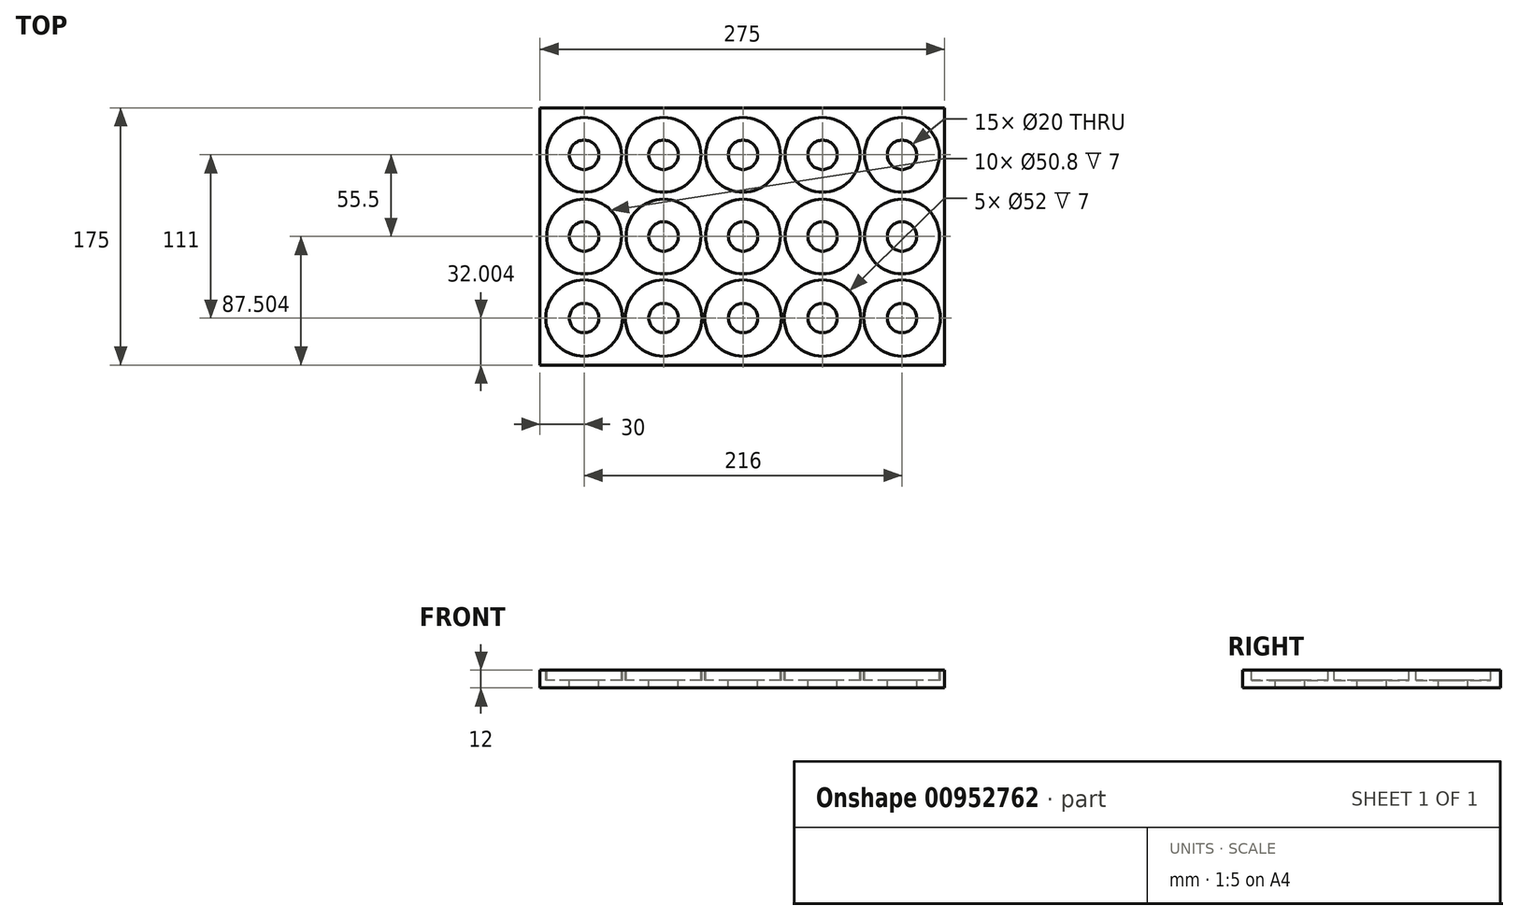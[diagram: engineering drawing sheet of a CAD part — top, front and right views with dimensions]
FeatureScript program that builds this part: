
annotation { "Feature Type Name" : "Feature", "Feature Type Description" : "" }
export const myFeature = defineFeature(function(context is Context, id is Id, definition is map)
    precondition{}
    {
        {
            var Q0;
            Q0=qCreatedBy(makeId("Top.planeOp"),FACE);
            var sketch = newSketch(context, id + "F0", { "sketchPlane" : qUnion([Q0])});
            skLineSegment(sketch, "E0.bottom", {"start": v(-57.94, 136.27) * mm, "end": v(217.06, 136.27) * mm});
            skLineSegment(sketch, "E0.top", {"start": v(-57.94, -38.73) * mm, "end": v(217.06, -38.73) * mm});
            skLineSegment(sketch, "E0.left", {"start": v(-57.94, 136.27) * mm, "end": v(-57.94, -38.73) * mm});
            skLineSegment(sketch, "E0.right", {"start": v(217.06, 136.27) * mm, "end": v(217.06, -38.73) * mm});
            skSolve(sketch);
        }
        {
            var Q0;
            Q0 = qSketchRegion(id + "F0", true);
            extrude(context, id + "F1", {"entities" : qUnion([Q0]), "depth" : 12 * mm, "offsetDistance" : 25 * mm});
        }
        {
            var Q0;
            Q0=makeQuery(id+"F1.opExtrude","CAP_FACE",FACE,{"disambiguationData":[OSD([sQuery(id+"F0.wireOp",EDGE,"E0.bottom"),sQuery(id+"F0.wireOp",EDGE,"E0.top"),sQuery(id+"F0.wireOp",EDGE,"E0.left"),sQuery(id+"F0.wireOp",EDGE,"E0.right")])],"isStart":false});
            var sketch = newSketch(context, id + "F2", { "sketchPlane" : qUnion([Q0])});
            skCircle(sketch, "E1", {"center": v(-27.94, 104.27) * mm, "radius": 25.4 * mm});
            skCircle(sketch, "E2", {"center": v(-27.94, 48.77) * mm, "radius": 25.4 * mm});
            skPoint(sketch, "E2.centerSnap0", {"position": v(-57.94, 48.77) * mm});
            skCircle(sketch, "E3", {"center": v(-27.94, -6.73) * mm, "radius": 26 * mm});
            skCircle(sketch, "E4", {"center": v(26.06, 104.27) * mm, "radius": 25.4 * mm});
            skCircle(sketch, "E5", {"center": v(26.06, 48.77) * mm, "radius": 25.4 * mm});
            skCircle(sketch, "E6", {"center": v(26.06, -6.73) * mm, "radius": 26 * mm});
            skCircle(sketch, "E7", {"center": v(80.06, 104.27) * mm, "radius": 25.4 * mm});
            skCircle(sketch, "E8", {"center": v(80.06, 48.77) * mm, "radius": 25.4 * mm});
            skCircle(sketch, "E9", {"center": v(80.06, -6.73) * mm, "radius": 26 * mm});
            skCircle(sketch, "E10", {"center": v(134.06, 104.27) * mm, "radius": 25.4 * mm});
            skCircle(sketch, "E11", {"center": v(134.06, 48.77) * mm, "radius": 25.4 * mm});
            skCircle(sketch, "E12", {"center": v(134.06, -6.73) * mm, "radius": 26 * mm});
            skCircle(sketch, "E13", {"center": v(188.06, 104.27) * mm, "radius": 25.4 * mm});
            skCircle(sketch, "E14", {"center": v(188.06, 48.77) * mm, "radius": 25.4 * mm});
            skCircle(sketch, "E15", {"center": v(188.06, -6.73) * mm, "radius": 26 * mm});
            skCircle(sketch, "E16", {"center": v(-27.94, 104.27) * mm, "radius": 10 * mm});
            skCircle(sketch, "E17", {"center": v(-27.94, 48.77) * mm, "radius": 10 * mm});
            skCircle(sketch, "E18", {"center": v(-27.94, -6.73) * mm, "radius": 10 * mm});
            skCircle(sketch, "E19", {"center": v(26.06, -6.73) * mm, "radius": 10 * mm});
            skCircle(sketch, "E20", {"center": v(26.06, 48.77) * mm, "radius": 10 * mm});
            skCircle(sketch, "E21", {"center": v(26.06, 104.27) * mm, "radius": 10 * mm});
            skCircle(sketch, "E22", {"center": v(80.06, 104.27) * mm, "radius": 10 * mm});
            skCircle(sketch, "E23", {"center": v(80.06, 48.77) * mm, "radius": 10 * mm});
            skCircle(sketch, "E24", {"center": v(80.06, -6.73) * mm, "radius": 10 * mm});
            skCircle(sketch, "E25", {"center": v(134.06, -6.73) * mm, "radius": 10 * mm});
            skCircle(sketch, "E26", {"center": v(188.06, -6.73) * mm, "radius": 10 * mm});
            skCircle(sketch, "E27", {"center": v(188.06, 48.77) * mm, "radius": 10 * mm});
            skCircle(sketch, "E28", {"center": v(134.06, 48.77) * mm, "radius": 10 * mm});
            skCircle(sketch, "E29", {"center": v(134.06, 104.27) * mm, "radius": 10 * mm});
            skCircle(sketch, "E30", {"center": v(188.06, 104.27) * mm, "radius": 10 * mm});
            skSolve(sketch);
        }
        {
            var Q0;
            Q0=makeQuery(id+"F2.imprint","IMPRINT",FACE,{"disambiguationData":[TD([[makeQuery(id+"F2.imprint","IMPRINT",EDGE,{"derivedFrom":sQuery(id+"F2.wireOp",EDGE,"E1")}),1.0]])]});
            var Q1;
            Q1=makeQuery(id+"F2.imprint","IMPRINT",FACE,{"disambiguationData":[TD([[makeQuery(id+"F2.imprint","IMPRINT",EDGE,{"derivedFrom":sQuery(id+"F2.wireOp",EDGE,"E2")}),1.0]])]});
            var Q2;
            Q2=makeQuery(id+"F2.imprint","IMPRINT",FACE,{"disambiguationData":[TD([[makeQuery(id+"F2.imprint","IMPRINT",EDGE,{"derivedFrom":sQuery(id+"F2.wireOp",EDGE,"E3")}),1.0]])]});
            var Q3;
            Q3=makeQuery(id+"F2.imprint","IMPRINT",FACE,{"disambiguationData":[TD([[makeQuery(id+"F2.imprint","IMPRINT",EDGE,{"derivedFrom":sQuery(id+"F2.wireOp",EDGE,"E6")}),1.0]])]});
            var Q4;
            Q4=makeQuery(id+"F2.imprint","IMPRINT",FACE,{"disambiguationData":[TD([[makeQuery(id+"F2.imprint","IMPRINT",EDGE,{"derivedFrom":sQuery(id+"F2.wireOp",EDGE,"E5")}),1.0]])]});
            var Q5;
            Q5=makeQuery(id+"F2.imprint","IMPRINT",FACE,{"disambiguationData":[TD([[makeQuery(id+"F2.imprint","IMPRINT",EDGE,{"derivedFrom":sQuery(id+"F2.wireOp",EDGE,"E4")}),1.0]])]});
            var Q6;
            Q6=makeQuery(id+"F2.imprint","IMPRINT",FACE,{"disambiguationData":[TD([[makeQuery(id+"F2.imprint","IMPRINT",EDGE,{"derivedFrom":sQuery(id+"F2.wireOp",EDGE,"E7")}),1.0]])]});
            var Q7;
            Q7=makeQuery(id+"F2.imprint","IMPRINT",FACE,{"disambiguationData":[TD([[makeQuery(id+"F2.imprint","IMPRINT",EDGE,{"derivedFrom":sQuery(id+"F2.wireOp",EDGE,"E8")}),1.0]])]});
            var Q8;
            Q8=makeQuery(id+"F2.imprint","IMPRINT",FACE,{"disambiguationData":[TD([[makeQuery(id+"F2.imprint","IMPRINT",EDGE,{"derivedFrom":sQuery(id+"F2.wireOp",EDGE,"E9")}),1.0]])]});
            var Q9;
            Q9=makeQuery(id+"F2.imprint","IMPRINT",FACE,{"disambiguationData":[TD([[makeQuery(id+"F2.imprint","IMPRINT",EDGE,{"derivedFrom":sQuery(id+"F2.wireOp",EDGE,"E12")}),1.0]])]});
            var Q10;
            Q10=makeQuery(id+"F2.imprint","IMPRINT",FACE,{"disambiguationData":[TD([[makeQuery(id+"F2.imprint","IMPRINT",EDGE,{"derivedFrom":sQuery(id+"F2.wireOp",EDGE,"E11")}),1.0]])]});
            var Q11;
            Q11=makeQuery(id+"F2.imprint","IMPRINT",FACE,{"disambiguationData":[TD([[makeQuery(id+"F2.imprint","IMPRINT",EDGE,{"derivedFrom":sQuery(id+"F2.wireOp",EDGE,"E10")}),1.0]])]});
            var Q12;
            Q12=makeQuery(id+"F2.imprint","IMPRINT",FACE,{"disambiguationData":[TD([[makeQuery(id+"F2.imprint","IMPRINT",EDGE,{"derivedFrom":sQuery(id+"F2.wireOp",EDGE,"E13")}),1.0]])]});
            var Q13;
            Q13=makeQuery(id+"F2.imprint","IMPRINT",FACE,{"disambiguationData":[TD([[makeQuery(id+"F2.imprint","IMPRINT",EDGE,{"derivedFrom":sQuery(id+"F2.wireOp",EDGE,"E14")}),1.0]])]});
            var Q14;
            Q14=makeQuery(id+"F2.imprint","IMPRINT",FACE,{"disambiguationData":[TD([[makeQuery(id+"F2.imprint","IMPRINT",EDGE,{"derivedFrom":sQuery(id+"F2.wireOp",EDGE,"E15")}),1.0]])]});
            extrude(context, id + "F3", {"entities" : qUnion([Q0, Q1, Q2, Q3, Q4, Q5, Q6, Q7, Q8, Q9, Q10, Q11, Q12, Q13, Q14]), "operationType" : NewBodyOperationType.REMOVE, "oppositeDirection" : true, "depth" : 7 * mm, "offsetDistance" : 25 * mm});
        }
        {
            var Q0;
            Q0=makeQuery(id+"F3.boolean.opBoolean","SPLIT",FACE,{"disambiguationData":[TD([makeQuery(id+"F3.opExtrude","SWEPT_FACE",FACE,{"disambiguationData":[OSD([sQuery(id+"F2.wireOp",EDGE,"E16")])]})])],"derivedFrom":makeQuery(id+"F1.opExtrude","CAP_FACE",FACE,{"disambiguationData":[OSD([sQuery(id+"F0.wireOp",EDGE,"E0.bottom"),sQuery(id+"F0.wireOp",EDGE,"E0.top"),sQuery(id+"F0.wireOp",EDGE,"E0.left"),sQuery(id+"F0.wireOp",EDGE,"E0.right")])],"isStart":false})});
            var Q1;
            Q1=makeQuery(id+"F3.boolean.opBoolean","SPLIT",FACE,{"disambiguationData":[TD([makeQuery(id+"F3.opExtrude","SWEPT_FACE",FACE,{"disambiguationData":[OSD([sQuery(id+"F2.wireOp",EDGE,"E21")])]})])],"derivedFrom":makeQuery(id+"F1.opExtrude","CAP_FACE",FACE,{"disambiguationData":[OSD([sQuery(id+"F0.wireOp",EDGE,"E0.bottom"),sQuery(id+"F0.wireOp",EDGE,"E0.top"),sQuery(id+"F0.wireOp",EDGE,"E0.left"),sQuery(id+"F0.wireOp",EDGE,"E0.right")])],"isStart":false})});
            var Q2;
            Q2=makeQuery(id+"F3.boolean.opBoolean","SPLIT",FACE,{"disambiguationData":[TD([makeQuery(id+"F3.opExtrude","SWEPT_FACE",FACE,{"disambiguationData":[OSD([sQuery(id+"F2.wireOp",EDGE,"E22")])]})])],"derivedFrom":makeQuery(id+"F1.opExtrude","CAP_FACE",FACE,{"disambiguationData":[OSD([sQuery(id+"F0.wireOp",EDGE,"E0.bottom"),sQuery(id+"F0.wireOp",EDGE,"E0.top"),sQuery(id+"F0.wireOp",EDGE,"E0.left"),sQuery(id+"F0.wireOp",EDGE,"E0.right")])],"isStart":false})});
            var Q3;
            Q3=makeQuery(id+"F3.boolean.opBoolean","SPLIT",FACE,{"disambiguationData":[TD([makeQuery(id+"F3.opExtrude","SWEPT_FACE",FACE,{"disambiguationData":[OSD([sQuery(id+"F2.wireOp",EDGE,"E29")])]})])],"derivedFrom":makeQuery(id+"F1.opExtrude","CAP_FACE",FACE,{"disambiguationData":[OSD([sQuery(id+"F0.wireOp",EDGE,"E0.bottom"),sQuery(id+"F0.wireOp",EDGE,"E0.top"),sQuery(id+"F0.wireOp",EDGE,"E0.left"),sQuery(id+"F0.wireOp",EDGE,"E0.right")])],"isStart":false})});
            var Q4;
            Q4=makeQuery(id+"F3.boolean.opBoolean","SPLIT",FACE,{"disambiguationData":[TD([makeQuery(id+"F3.opExtrude","SWEPT_FACE",FACE,{"disambiguationData":[OSD([sQuery(id+"F2.wireOp",EDGE,"E30")])]})])],"derivedFrom":makeQuery(id+"F1.opExtrude","CAP_FACE",FACE,{"disambiguationData":[OSD([sQuery(id+"F0.wireOp",EDGE,"E0.bottom"),sQuery(id+"F0.wireOp",EDGE,"E0.top"),sQuery(id+"F0.wireOp",EDGE,"E0.left"),sQuery(id+"F0.wireOp",EDGE,"E0.right")])],"isStart":false})});
            var Q5;
            Q5=makeQuery(id+"F3.boolean.opBoolean","SPLIT",FACE,{"disambiguationData":[TD([makeQuery(id+"F3.opExtrude","SWEPT_FACE",FACE,{"disambiguationData":[OSD([sQuery(id+"F2.wireOp",EDGE,"E27")])]})])],"derivedFrom":makeQuery(id+"F1.opExtrude","CAP_FACE",FACE,{"disambiguationData":[OSD([sQuery(id+"F0.wireOp",EDGE,"E0.bottom"),sQuery(id+"F0.wireOp",EDGE,"E0.top"),sQuery(id+"F0.wireOp",EDGE,"E0.left"),sQuery(id+"F0.wireOp",EDGE,"E0.right")])],"isStart":false})});
            var Q6;
            Q6=makeQuery(id+"F3.boolean.opBoolean","SPLIT",FACE,{"disambiguationData":[TD([makeQuery(id+"F3.opExtrude","SWEPT_FACE",FACE,{"disambiguationData":[OSD([sQuery(id+"F2.wireOp",EDGE,"E28")])]})])],"derivedFrom":makeQuery(id+"F1.opExtrude","CAP_FACE",FACE,{"disambiguationData":[OSD([sQuery(id+"F0.wireOp",EDGE,"E0.bottom"),sQuery(id+"F0.wireOp",EDGE,"E0.top"),sQuery(id+"F0.wireOp",EDGE,"E0.left"),sQuery(id+"F0.wireOp",EDGE,"E0.right")])],"isStart":false})});
            var Q7;
            Q7=makeQuery(id+"F3.boolean.opBoolean","SPLIT",FACE,{"disambiguationData":[TD([makeQuery(id+"F3.opExtrude","SWEPT_FACE",FACE,{"disambiguationData":[OSD([sQuery(id+"F2.wireOp",EDGE,"E23")])]})])],"derivedFrom":makeQuery(id+"F1.opExtrude","CAP_FACE",FACE,{"disambiguationData":[OSD([sQuery(id+"F0.wireOp",EDGE,"E0.bottom"),sQuery(id+"F0.wireOp",EDGE,"E0.top"),sQuery(id+"F0.wireOp",EDGE,"E0.left"),sQuery(id+"F0.wireOp",EDGE,"E0.right")])],"isStart":false})});
            var Q8;
            Q8=makeQuery(id+"F3.boolean.opBoolean","SPLIT",FACE,{"disambiguationData":[TD([makeQuery(id+"F3.opExtrude","SWEPT_FACE",FACE,{"disambiguationData":[OSD([sQuery(id+"F2.wireOp",EDGE,"E20")])]})])],"derivedFrom":makeQuery(id+"F1.opExtrude","CAP_FACE",FACE,{"disambiguationData":[OSD([sQuery(id+"F0.wireOp",EDGE,"E0.bottom"),sQuery(id+"F0.wireOp",EDGE,"E0.top"),sQuery(id+"F0.wireOp",EDGE,"E0.left"),sQuery(id+"F0.wireOp",EDGE,"E0.right")])],"isStart":false})});
            var Q9;
            Q9=makeQuery(id+"F3.boolean.opBoolean","SPLIT",FACE,{"disambiguationData":[TD([makeQuery(id+"F3.opExtrude","SWEPT_FACE",FACE,{"disambiguationData":[OSD([sQuery(id+"F2.wireOp",EDGE,"E17")])]})])],"derivedFrom":makeQuery(id+"F1.opExtrude","CAP_FACE",FACE,{"disambiguationData":[OSD([sQuery(id+"F0.wireOp",EDGE,"E0.bottom"),sQuery(id+"F0.wireOp",EDGE,"E0.top"),sQuery(id+"F0.wireOp",EDGE,"E0.left"),sQuery(id+"F0.wireOp",EDGE,"E0.right")])],"isStart":false})});
            var Q10;
            Q10=makeQuery(id+"F3.boolean.opBoolean","SPLIT",FACE,{"disambiguationData":[TD([makeQuery(id+"F3.opExtrude","SWEPT_FACE",FACE,{"disambiguationData":[OSD([sQuery(id+"F2.wireOp",EDGE,"E18")])]})])],"derivedFrom":makeQuery(id+"F1.opExtrude","CAP_FACE",FACE,{"disambiguationData":[OSD([sQuery(id+"F0.wireOp",EDGE,"E0.bottom"),sQuery(id+"F0.wireOp",EDGE,"E0.top"),sQuery(id+"F0.wireOp",EDGE,"E0.left"),sQuery(id+"F0.wireOp",EDGE,"E0.right")])],"isStart":false})});
            var Q11;
            Q11=makeQuery(id+"F3.boolean.opBoolean","SPLIT",FACE,{"disambiguationData":[TD([makeQuery(id+"F3.opExtrude","SWEPT_FACE",FACE,{"disambiguationData":[OSD([sQuery(id+"F2.wireOp",EDGE,"E19")])]})])],"derivedFrom":makeQuery(id+"F1.opExtrude","CAP_FACE",FACE,{"disambiguationData":[OSD([sQuery(id+"F0.wireOp",EDGE,"E0.bottom"),sQuery(id+"F0.wireOp",EDGE,"E0.top"),sQuery(id+"F0.wireOp",EDGE,"E0.left"),sQuery(id+"F0.wireOp",EDGE,"E0.right")])],"isStart":false})});
            var Q12;
            Q12=makeQuery(id+"F3.boolean.opBoolean","SPLIT",FACE,{"disambiguationData":[TD([makeQuery(id+"F3.opExtrude","SWEPT_FACE",FACE,{"disambiguationData":[OSD([sQuery(id+"F2.wireOp",EDGE,"E24")])]})])],"derivedFrom":makeQuery(id+"F1.opExtrude","CAP_FACE",FACE,{"disambiguationData":[OSD([sQuery(id+"F0.wireOp",EDGE,"E0.bottom"),sQuery(id+"F0.wireOp",EDGE,"E0.top"),sQuery(id+"F0.wireOp",EDGE,"E0.left"),sQuery(id+"F0.wireOp",EDGE,"E0.right")])],"isStart":false})});
            var Q13;
            Q13=makeQuery(id+"F3.boolean.opBoolean","SPLIT",FACE,{"disambiguationData":[TD([makeQuery(id+"F3.opExtrude","SWEPT_FACE",FACE,{"disambiguationData":[OSD([sQuery(id+"F2.wireOp",EDGE,"E25")])]})])],"derivedFrom":makeQuery(id+"F1.opExtrude","CAP_FACE",FACE,{"disambiguationData":[OSD([sQuery(id+"F0.wireOp",EDGE,"E0.bottom"),sQuery(id+"F0.wireOp",EDGE,"E0.top"),sQuery(id+"F0.wireOp",EDGE,"E0.left"),sQuery(id+"F0.wireOp",EDGE,"E0.right")])],"isStart":false})});
            var Q14;
            Q14=makeQuery(id+"F3.boolean.opBoolean","SPLIT",FACE,{"disambiguationData":[TD([makeQuery(id+"F3.opExtrude","SWEPT_FACE",FACE,{"disambiguationData":[OSD([sQuery(id+"F2.wireOp",EDGE,"E26")])]})])],"derivedFrom":makeQuery(id+"F1.opExtrude","CAP_FACE",FACE,{"disambiguationData":[OSD([sQuery(id+"F0.wireOp",EDGE,"E0.bottom"),sQuery(id+"F0.wireOp",EDGE,"E0.top"),sQuery(id+"F0.wireOp",EDGE,"E0.left"),sQuery(id+"F0.wireOp",EDGE,"E0.right")])],"isStart":false})});
            extrude(context, id + "F4", {"entities" : qUnion([Q0, Q1, Q2, Q3, Q4, Q5, Q6, Q7, Q8, Q9, Q10, Q11, Q12, Q13, Q14]), "operationType" : NewBodyOperationType.REMOVE, "oppositeDirection" : true, "depth" : 25 * mm, "offsetDistance" : 25 * mm});
        }
    });
